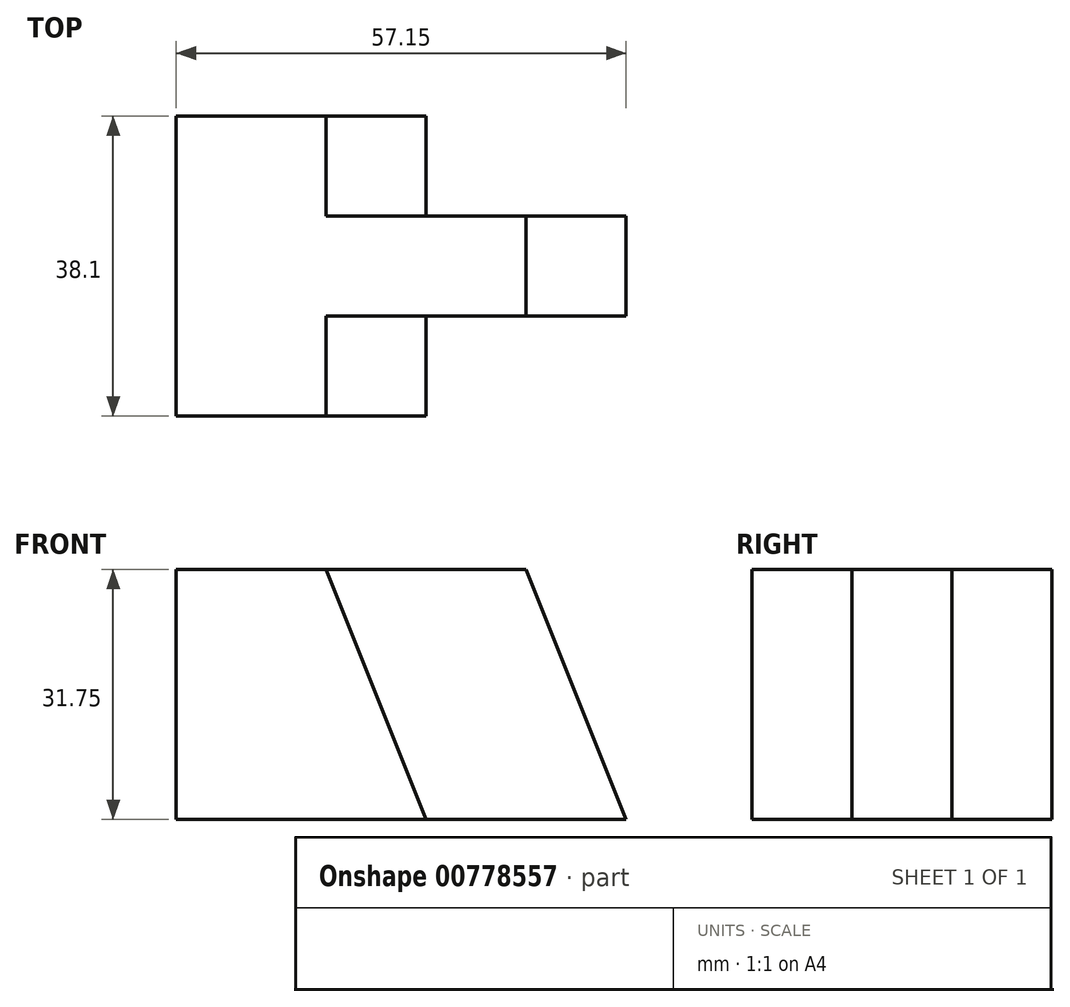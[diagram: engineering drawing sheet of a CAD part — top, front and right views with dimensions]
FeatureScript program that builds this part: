
annotation { "Feature Type Name" : "Feature", "Feature Type Description" : "" }
export const myFeature = defineFeature(function(context is Context, id is Id, definition is map)
    precondition{}
    {
        {
            var Q0;
            Q0=qCreatedBy(makeId("Front.planeOp"),FACE);
            var sketch = newSketch(context, id + "F0", { "sketchPlane" : qUnion([Q0])});
            skLineSegment(sketch, "E0", {"start": v(0, 0) * mm, "end": v(57.15, 0) * mm});
            skLineSegment(sketch, "E1", {"start": v(57.15, 0) * mm, "end": v(57.15, 31.75) * mm});
            skLineSegment(sketch, "E2", {"start": v(57.15, 31.75) * mm, "end": v(0, 31.75) * mm});
            skLineSegment(sketch, "E3", {"start": v(0, 31.75) * mm, "end": v(0, 0) * mm});
            skSolve(sketch);
        }
        {
            var Q0;
            Q0=makeQuery(id+"F0.imprint","IMPRINT",FACE,{"disambiguationData":[TD([[makeQuery(id+"F0.imprint","IMPRINT",EDGE,{"derivedFrom":sQuery(id+"F0.wireOp",EDGE,"E0")}),1.0]])]});
            extrude(context, id + "F1", {"entities" : qUnion([Q0]), "depth" : 38.1 * mm, "offsetDistance" : 25.4 * mm});
        }
        {
            var Q0;
            Q0=makeQuery(id+"F1.opExtrude","CAP_FACE",FACE,{"disambiguationData":[OSD([sQuery(id+"F0.wireOp",EDGE,"E0"),sQuery(id+"F0.wireOp",EDGE,"E1"),sQuery(id+"F0.wireOp",EDGE,"E2"),sQuery(id+"F0.wireOp",EDGE,"E3")])],"isStart":false});
            var sketch = newSketch(context, id + "F2", { "sketchPlane" : qUnion([Q0])});
            skLineSegment(sketch, "E4", {"start": v(0, 31.75) * mm, "end": v(19.05, 31.75) * mm});
            skLineSegment(sketch, "E5", {"start": v(0, 0) * mm, "end": v(31.75, 0) * mm});
            skLineSegment(sketch, "E6", {"start": v(19.05, 31.75) * mm, "end": v(31.75, 0) * mm});
            skSolve(sketch);
        }
        {
            var Q0;
            {var subQ0=sQuery(id+"F2.wireOp",EDGE,"E6");Q0=makeQuery(id+"F2.imprint","IMPRINT",FACE,{"disambiguationData":[TD([[makeQuery(id+"F2.imprint","IMPRINT",EDGE,{"derivedFrom":subQ0}),1.0]])]});}
            extrude(context, id + "F3", {"entities" : qUnion([Q0]), "operationType" : NewBodyOperationType.REMOVE, "oppositeDirection" : true, "depth" : 12.7 * mm, "offsetDistance" : 25.4 * mm});
        }
        {
            var Q0;
            Q0=makeQuery(id+"F1.opExtrude","CAP_FACE",FACE,{"disambiguationData":[OSD([sQuery(id+"F0.wireOp",EDGE,"E0"),sQuery(id+"F0.wireOp",EDGE,"E1"),sQuery(id+"F0.wireOp",EDGE,"E2"),sQuery(id+"F0.wireOp",EDGE,"E3")])],"isStart":true});
            var sketch = newSketch(context, id + "F4", { "sketchPlane" : qUnion([Q0])});
            skLineSegment(sketch, "E7", {"start": v(0, 0) * mm, "end": v(-31.75, 0) * mm});
            skLineSegment(sketch, "E8", {"start": v(0, 31.75) * mm, "end": v(-19.05, 31.75) * mm});
            skLineSegment(sketch, "E9", {"start": v(-19.05, 31.75) * mm, "end": v(-31.75, 0) * mm});
            skSolve(sketch);
        }
        {
            var Q0;
            {var subQ0=sQuery(id+"F4.wireOp",EDGE,"E9");Q0=makeQuery(id+"F4.imprint","IMPRINT",FACE,{"disambiguationData":[TD([[makeQuery(id+"F4.imprint","IMPRINT",EDGE,{"derivedFrom":subQ0}),-1.0]])]});}
            extrude(context, id + "F5", {"entities" : qUnion([Q0]), "operationType" : NewBodyOperationType.REMOVE, "oppositeDirection" : true, "depth" : 12.7 * mm, "offsetDistance" : 25.4 * mm});
        }
        {
            var Q0;
            Q0=makeQuery(id+"F3.boolean.opBoolean","COPY",FACE,{"derivedFrom":makeQuery(id+"F3.opExtrude","CAP_FACE",FACE,{"disambiguationData":[OSD([sQuery(id+"F0.wireOp",EDGE,"E0"),sQuery(id+"F0.wireOp",EDGE,"E1"),sQuery(id+"F0.wireOp",EDGE,"E2"),sQuery(id+"F2.wireOp",EDGE,"E6")])],"isStart":false})});
            var sketch = newSketch(context, id + "F6", { "sketchPlane" : qUnion([Q0])});
            skLineSegment(sketch, "E10", {"start": v(19.05, 31.75) * mm, "end": v(44.45, 31.75) * mm});
            skLineSegment(sketch, "E11", {"start": v(31.75, 0) * mm, "end": v(57.15, 0) * mm});
            skLineSegment(sketch, "E12", {"start": v(44.45, 31.75) * mm, "end": v(57.15, 0) * mm});
            skSolve(sketch);
        }
        {
            var Q0;
            {var subQ0=sQuery(id+"F6.wireOp",EDGE,"E12");Q0=makeQuery(id+"F6.imprint","IMPRINT",FACE,{"disambiguationData":[TD([[makeQuery(id+"F6.imprint","IMPRINT",EDGE,{"derivedFrom":subQ0}),1.0]])]});}
            extrude(context, id + "F7", {"entities" : qUnion([Q0]), "operationType" : NewBodyOperationType.REMOVE, "oppositeDirection" : true, "depth" : 12.7 * mm, "offsetDistance" : 25.4 * mm});
        }
    });
